# Revit family: Hand_Shower-Grohe-Euphoria_110_27239001
name_source: partatom
category: Plumbing Fixtures
units: mm (PartAtom-declared; Revit-internal decimal feet)

## family parameters
Always vertical = No
Cut with Voids When Loaded = No
OmniClass Number = 23.45.05.14.17
OmniClass Title = Showers
Part Type = Normal
Room Calculation Point = No
Round Connector Dimension = Use Diameter
Shared = Yes
Work Plane-Based = Yes

## types (1)
- 27239001
    Assembly Code = D2010710
    CW Connection = Yes
    CWFU = 3
    Cold Water Connection Diameter = 1/2"
    Cold Water Connection Radius = 1/4"
    Default Elevation = 0"
    Description = Euphoria 110 Massage Handshower 3 sprays
    Finish = Metal-Grohe-000-StarLight Chrome
    Flow Rate = 2.5 gpm (9.5 L/min)
    HW Connection = Yes
    HWFU = 3
    Height = 7 7/16"
    Hot Water Connection Diameter = 1"
    Hot Water Connection Radius = 1/4"
    Manufacturer = Grohe
    Material = Metal-Grohe-000-StarLight Chrome
    Model = 27239001
    Price = Prices may vary. Please consult Manufacturer Representative for most up-to-date price list.
    Product Documentation Link = https://americanstandard.box.com
    Product Page URL = https://www.grohe.us
    Tempered Connection Diameter = 1/2"
    Tempered Connection Radius = 1/4"
    URL = https://www.grohe.us
    Vent Connection = No
    WFU = 4
    Warranty Documentation Link = https://cdn.cloud.grohe.com
    Waste Connection = No
    cUPC Compliant = Yes

## geometry (parser evidence)
native form markers: Sweep x2
no freeform markers — native parametric forms only
